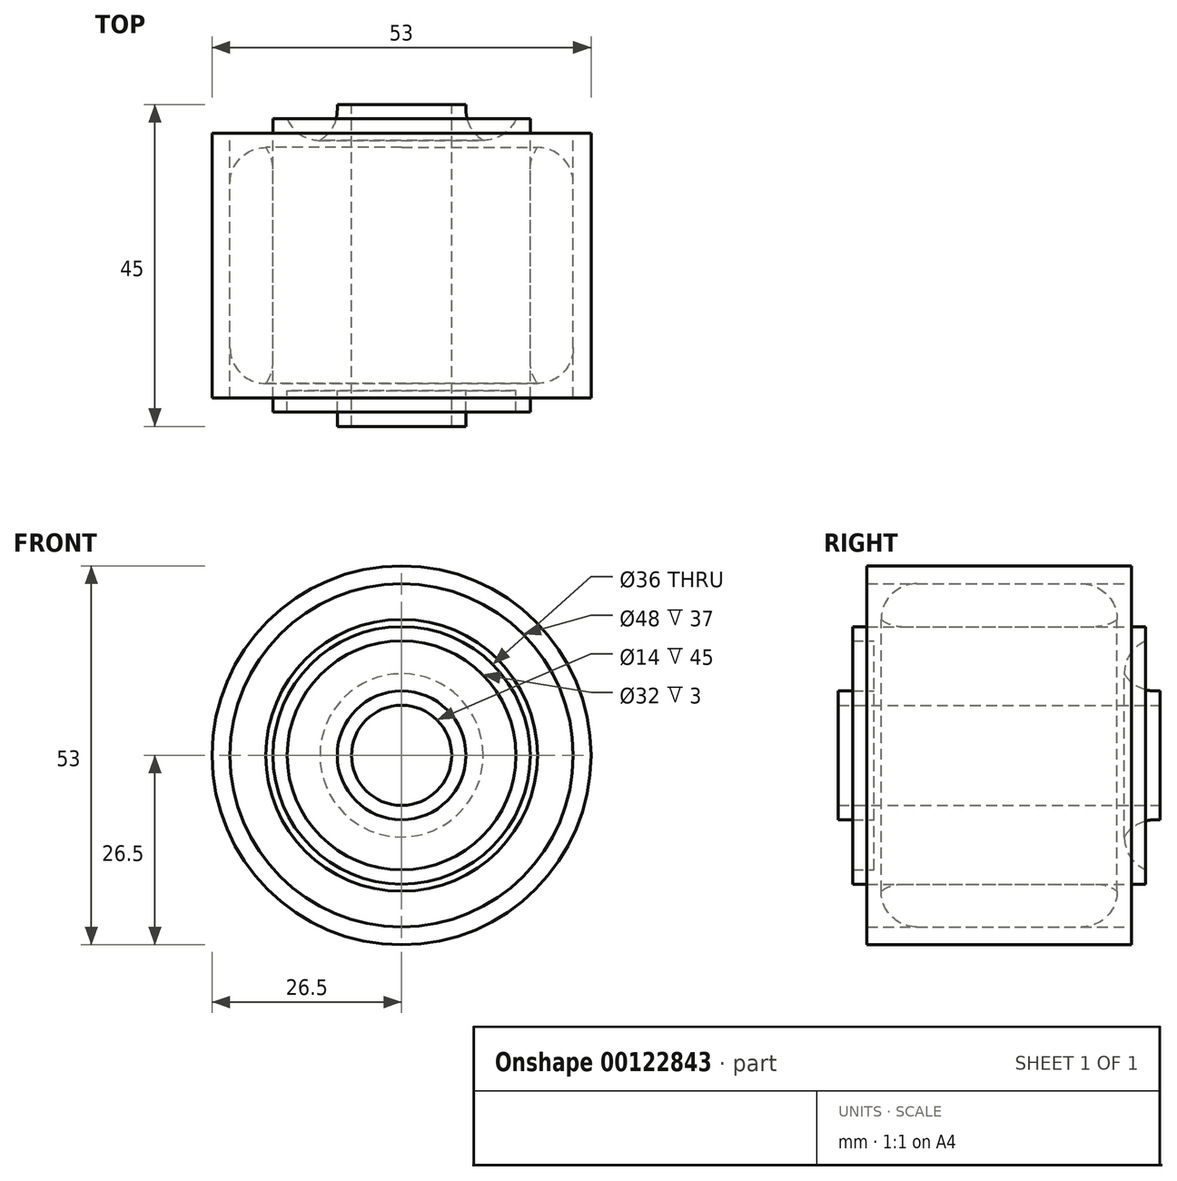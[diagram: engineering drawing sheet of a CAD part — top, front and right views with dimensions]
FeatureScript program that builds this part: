
annotation { "Feature Type Name" : "Feature", "Feature Type Description" : "" }
export const myFeature = defineFeature(function(context is Context, id is Id, definition is map)
    precondition{}
    {
        {
            var Q0;
            Q0=qCreatedBy(makeId("Front.planeOp"),FACE);
            var sketch = newSketch(context, id + "F0", { "sketchPlane" : qUnion([Q0])});
            skCircle(sketch, "E0", {"center": v(0, 0) * mm, "radius": 7 * mm});
            skCircle(sketch, "E1", {"center": v(0, 0) * mm, "radius": 9 * mm});
            skSolve(sketch);
        }
        {
            var Q0;
            Q0 = qSketchRegion(id + "F0", true);
            extrude(context, id + "F1", {"entities" : qUnion([Q0]), "depth" : 45 * mm});
        }
        {
            var Q0;
            Q0=qCreatedBy(makeId("Front.planeOp"),FACE);
            cPlane(context, id + "F2", {"entities" : qUnion([Q0]), "cplaneType" : CPlaneType.OFFSET, "offset" : 5 * mm, "width" : 150 * mm, "height" : 150 * mm});
        }
        {
            var Q0;
            Q0=qCreatedBy(id+"F2.planeOp",FACE);
            var sketch = newSketch(context, id + "F3", { "sketchPlane" : qUnion([Q0])});
            skCircle(sketch, "E2", {"center": v(0, 0) * mm, "radius": 9 * mm});
            skCircle(sketch, "E3", {"center": v(0, 0) * mm, "radius": 16 * mm});
            skSolve(sketch);
        }
        {
            var Q0;
            Q0 = qSketchRegion(id + "F3", true);
            var Q1;
            Q1=makeQuery(id+"F3.imprint","IMPRINT",FACE,{"disambiguationData":[TD([[makeQuery(id+"F3.imprint","IMPRINT",EDGE,{"derivedFrom":sQuery(id+"F3.wireOp",EDGE,"E2")}),-1.0]])]});
            extrude(context, id + "F4", {"entities" : qUnion([Q0, Q1]), "operationType" : NewBodyOperationType.ADD, "depth" : 35 * mm});
        }
        {
            var Q0;
            Q0=qCreatedBy(makeId("Front.planeOp"),FACE);
            cPlane(context, id + "F5", {"entities" : qUnion([Q0]), "cplaneType" : CPlaneType.OFFSET, "offset" : 2 * mm, "width" : 150 * mm, "height" : 150 * mm});
        }
        {
            var Q0;
            Q0=qCreatedBy(id+"F5.planeOp",FACE);
            var sketch = newSketch(context, id + "F6", { "sketchPlane" : qUnion([Q0])});
            skCircle(sketch, "E4", {"center": v(0, 0) * mm, "radius": 16 * mm});
            skCircle(sketch, "E5", {"center": v(0, 0) * mm, "radius": 18 * mm});
            skSolve(sketch);
        }
        {
            var Q0;
            Q0 = qSketchRegion(id + "F6", true);
            extrude(context, id + "F7", {"entities" : qUnion([Q0]), "operationType" : NewBodyOperationType.ADD, "depth" : 41 * mm});
        }
        {
            var Q0;
            Q0=qCreatedBy(makeId("Front.planeOp"),FACE);
            cPlane(context, id + "F8", {"entities" : qUnion([Q0]), "cplaneType" : CPlaneType.OFFSET, "offset" : 4 * mm, "width" : 150 * mm, "height" : 150 * mm});
        }
        {
            var Q0;
            Q0=qCreatedBy(id+"F8.planeOp",FACE);
            var sketch = newSketch(context, id + "F9", { "sketchPlane" : qUnion([Q0])});
            skCircle(sketch, "E6", {"center": v(0, 0) * mm, "radius": 24 * mm});
            skCircle(sketch, "E7", {"center": v(0, 0) * mm, "radius": 26.5 * mm});
            skSolve(sketch);
        }
        {
            var Q0;
            Q0 = qSketchRegion(id + "F9", true);
            extrude(context, id + "F10", {"entities" : qUnion([Q0]), "depth" : 37 * mm});
        }
        {
            var Q0;
            Q0=qCreatedBy(makeId("Front.planeOp"),FACE);
            cPlane(context, id + "F11", {"entities" : qUnion([Q0]), "cplaneType" : CPlaneType.OFFSET, "offset" : 6 * mm, "width" : 150 * mm, "height" : 150 * mm});
        }
        {
            var Q0;
            Q0=qCreatedBy(id+"F11.planeOp",FACE);
            var sketch = newSketch(context, id + "F12", { "sketchPlane" : qUnion([Q0])});
            skCircle(sketch, "E8", {"center": v(0, 0) * mm, "radius": 18 * mm});
            skCircle(sketch, "E9", {"center": v(0, 0) * mm, "radius": 24 * mm});
            skSolve(sketch);
        }
        {
            var Q0;
            Q0 = qSketchRegion(id + "F12", true);
            extrude(context, id + "F13", {"entities" : qUnion([Q0]), "depth" : 33 * mm});
        }
        {
            var Q0;
            Q0=makeQuery(id+"F4.opExtrude","CAP_EDGE",EDGE,{"disambiguationData":[OSD([sQuery(id+"F3.wireOp",EDGE,"E3")])],"isStart":false});
            var Q1;
            Q1=makeQuery(id+"F13.opExtrude","CAP_EDGE",EDGE,{"disambiguationData":[OSD([sQuery(id+"F12.wireOp",EDGE,"E9")])],"isStart":false});
            fillet(context, id + "F14", {"entities" : qUnion([Q0, Q1]), "radius" : 5 * mm, "tangentPropagation" : true, "allowEdgeOverflow" : false});
        }
        {
            var Q0;
            Q0=makeQuery(id+"F4.opExtrude","CAP_EDGE",EDGE,{"disambiguationData":[OSD([sQuery(id+"F3.wireOp",EDGE,"E2")])],"isStart":false});
            var Q1;
            Q1=makeQuery(id+"F13.opExtrude","CAP_EDGE",EDGE,{"disambiguationData":[OSD([sQuery(id+"F12.wireOp",EDGE,"E8")])],"isStart":false});
            fillet(context, id + "F15", {"entities" : qUnion([Q0, Q1]), "radius" : 5 * mm, "tangentPropagation" : true, "allowEdgeOverflow" : false});
        }
        {
            var Q0;
            Q0=makeQuery(id+"F4.opExtrude","CAP_EDGE",EDGE,{"disambiguationData":[OSD([sQuery(id+"F3.wireOp",EDGE,"E3")])],"isStart":true});
            var Q1;
            Q1=makeQuery(id+"F13.opExtrude","CAP_EDGE",EDGE,{"disambiguationData":[OSD([sQuery(id+"F12.wireOp",EDGE,"E9")])],"isStart":true});
            fillet(context, id + "F16", {"entities" : qUnion([Q0, Q1]), "radius" : 5 * mm, "tangentPropagation" : true, "allowEdgeOverflow" : false});
        }
        {
            var Q0;
            Q0=makeQuery(id+"F4.opExtrude","CAP_EDGE",EDGE,{"disambiguationData":[OSD([sQuery(id+"F3.wireOp",EDGE,"E2")])],"isStart":true});
            var Q1;
            Q1=makeQuery(id+"F13.opExtrude","CAP_EDGE",EDGE,{"disambiguationData":[OSD([sQuery(id+"F12.wireOp",EDGE,"E8")])],"isStart":true});
            fillet(context, id + "F17", {"entities" : qUnion([Q0, Q1]), "radius" : 5 * mm, "tangentPropagation" : true, "allowEdgeOverflow" : false});
        }
    });
